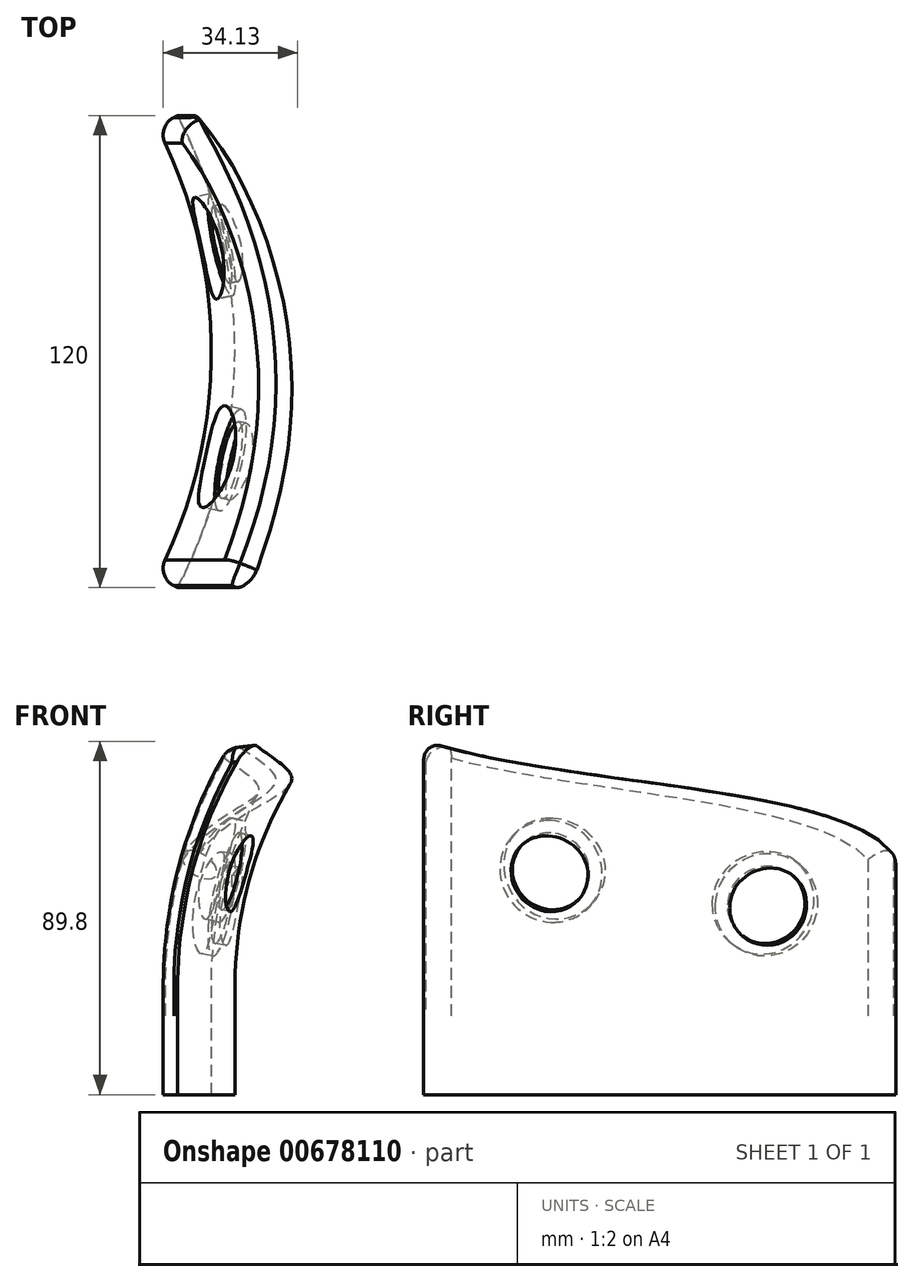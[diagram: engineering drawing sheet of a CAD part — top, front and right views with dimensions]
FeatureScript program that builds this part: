
annotation { "Feature Type Name" : "Feature", "Feature Type Description" : "" }
export const myFeature = defineFeature(function(context is Context, id is Id, definition is map)
    precondition{}
    {
        {
            var Q0;
            Q0=qCreatedBy(makeId("Top.planeOp"),FACE);
            var sketch = newSketch(context, id + "F0", { "sketchPlane" : qUnion([Q0])});
            skCircle(sketch, "E0", {"center": v(0, 0) * mm, "radius": 125 * mm});
            skCircle(sketch, "E1", {"center": v(0, 0) * mm, "radius": 131 * mm});
            skLineSegment(sketch, "E2", {"start": v(0, 0) * mm, "end": v(116.45, 60) * mm});
            skLineSegment(sketch, "E3", {"start": v(0, 0) * mm, "end": v(116.45, -60) * mm});
            skLineSegment(sketch, "E4", {"start": v(116.45, -60) * mm, "end": v(116.45, 60) * mm, "construction": true});
            skPoint(sketch, "E5", {"position": v(125, 0) * mm});
            skLineSegment(sketch, "E6", {"start": v(0, 0) * mm, "end": v(167.42, 0) * mm, "construction": true});
            skPoint(sketch, "E6.endSnap0", {"position": v(116.45, 0) * mm});
            skLineSegment(sketch, "E7", {"start": v(0, 0) * mm, "end": v(290.04, 61.65) * mm, "construction": true});
            skLineSegment(sketch, "E8", {"start": v(0, 0) * mm, "end": v(279.85, -59.48) * mm, "construction": true});
            skLineSegment(sketch, "E9", {"start": v(0, 0) * mm, "end": v(22.15, 104.2) * mm, "construction": true});
            skLineSegment(sketch, "E10", {"start": v(0, 0) * mm, "end": v(-22.73, 106.95) * mm, "construction": true});
            skSolve(sketch);
        }
        {
            var Q0;
            Q0=qCreatedBy(makeId("Front.planeOp"),FACE);
            var sketch = newSketch(context, id + "F1", { "sketchPlane" : qUnion([Q0])});
            skLineSegment(sketch, "E11.0", {"start": v(-125, 0) * mm, "end": v(125, 0) * mm, "construction": true});
            skLineSegment(sketch, "E12.0", {"start": v(-131, 0) * mm, "end": v(131, 0) * mm, "construction": true});
            skPoint(sketch, "E13.0", {"position": v(116.45, 0) * mm});
            skLineSegment(sketch, "E14", {"start": v(125, 0) * mm, "end": v(131, 0) * mm, "construction": true});
            skPoint(sketch, "E15", {"position": v(128, 0) * mm});
            skFitSpline(sketch, "E16", {"points": [v(128, 0) * mm, v(128, 5.95) * mm, v(153, 75) * mm], "startDerivative": vector(0, 39.53) * mm, "endDerivative": vector(96.35, 111.36) * mm});
            skLineSegment(sketch, "E17", {"start": v(128, 0) * mm, "end": v(128, 92.21) * mm, "construction": true});
            skLineSegment(sketch, "E18", {"start": v(128, 0) * mm, "end": v(128, -20) * mm, "construction": true});
            skLineSegment(sketch, "E19", {"start": v(149.6, 60.4) * mm, "end": v(80.14, 60.4) * mm, "construction": true});
            skLineSegment(sketch, "E20", {"start": v(128, 0) * mm, "end": v(153, 75) * mm, "construction": true});
            skLineSegment(sketch, "E21", {"start": v(135.36, 46.04) * mm, "end": v(0, 99.87) * mm, "construction": true});
            skLineSegment(sketch, "E22", {"start": v(0, 0) * mm, "end": v(0, 121.22) * mm, "construction": true});
            skLineSegment(sketch, "E23", {"start": v(0, 0) * mm, "end": v(20.37, 115.5) * mm, "construction": true});
            skPoint(sketch, "E24", {"position": v(135.36, 46.04) * mm});
            skLineSegment(sketch, "E25", {"start": v(135.36, 46.04) * mm, "end": v(125, 20) * mm, "construction": true});
            skPoint(sketch, "E26", {"position": v(128.4, 16.37) * mm});
            skLineSegment(sketch, "E27", {"start": v(128.4, 16.37) * mm, "end": v(127.55, 6.42) * mm, "construction": true});
            skLineSegment(sketch, "E28", {"start": v(128.4, 16.37) * mm, "end": v(0, 27.32) * mm, "construction": true});
            skLineSegment(sketch, "E29", {"start": v(0, 0) * mm, "end": v(28.87, 125.04) * mm, "construction": true});
            skSolve(sketch);
        }
        {
            var Q0;
            {var subQ0=sQuery(id+"F0.wireOp",EDGE,"E2");var subQ1=sQuery(id+"F0.wireOp",EDGE,"E0");var subQ2=makeQuery(id+"F0.imprint","INTERSECT",VERTEX,{"derivedFrom":[subQ1,subQ0]});Q0=makeQuery(id+"F0.imprint","IMPRINT",FACE,{"disambiguationData":[TD([[makeQuery(id+"F0.imprint","IMPRINT",EDGE,{"disambiguationData":[TD([[subQ2,1.0]])],"derivedFrom":subQ1}),-1.0]])]});}
            var Q1;
            Q1=sQuery(id+"F1.wireOp",EDGE,"E16");
            sweep(context, id + "F2", {"profiles" : qUnion([Q0]), "path" : qUnion([Q1])});
        }
        {
            var Q0;
            Q0=makeQuery(id+"F2.opSweep","SWEPT_EDGE",EDGE,{"disambiguationData":[OSD([sQuery(id+"F0.wireOp",EDGE,"E1"),sQuery(id+"F0.wireOp",EDGE,"E3"),sQuery(id+"F1.wireOp",EDGE,"E16")])]});
            cPoint(context, id + "F3", {"entities" : qUnion([Q0]), "parameter" : 0.5});
        }
        {
            var Q0;
            Q0=qCreatedBy(makeId("Front.planeOp"),FACE);
            var Q1;
            Q1=qCreatedBy(id+"F3",VERTEX);
            cPlane(context, id + "F4", {"entities" : qUnion([Q0, Q1]), "cplaneType" : CPlaneType.PLANE_POINT, "offset" : 25 * mm, "width" : 150 * mm, "height" : 150 * mm});
        }
        {
            var Q0;
            Q0=qCreatedBy(id+"F4.planeOp",FACE);
            var sketch = newSketch(context, id + "F5", { "sketchPlane" : qUnion([Q0])});
            skLineSegment(sketch, "E30", {"start": v(16.14, 70) * mm, "end": v(342.74, 70) * mm});
            skLineSegment(sketch, "E31.top", {"start": v(16.14, 220) * mm, "end": v(342.74, 220) * mm});
            skLineSegment(sketch, "E31.left", {"start": v(16.14, 70) * mm, "end": v(16.14, 220) * mm});
            skLineSegment(sketch, "E31.right", {"start": v(342.74, 70) * mm, "end": v(342.74, 220) * mm});
            skSolve(sketch);
        }
        {
            var Q0;
            Q0=qCreatedBy(makeId("Right.planeOp"),FACE);
            var sketch = newSketch(context, id + "F6", { "sketchPlane" : qUnion([Q0])});
            skPoint(sketch, "E32.0", {"position": v(-60, 70) * mm});
            skLineSegment(sketch, "E33", {"start": v(-74, 70) * mm, "end": v(-141.5, 70) * mm, "construction": true});
            skFitSpline(sketch, "E34.0", {"points": [v(50, 0) * mm, v(1000, 50) * mm, v(2.92, 1000) * mm, v(50, 3.5) * mm, v(1000, 50) * mm, v(7.03, 1000) * mm, v(50, 8.56) * mm, v(1000, 50) * mm, v(12.28, 1000) * mm, v(50, 14.48) * mm, v(1000, 50) * mm, v(21.9, 1000) * mm], "construction": true});
            skFitSpline(sketch, "E35.0", {"points": [v(-50, 0) * mm, v(1000, -50) * mm, v(2.92, 1000) * mm, v(-50, 3.5) * mm, v(1000, -50) * mm, v(7.03, 1000) * mm, v(-50, 8.56) * mm, v(1000, -50) * mm, v(12.28, 1000) * mm, v(-50, 14.48) * mm, v(1000, -50) * mm, v(21.9, 1000) * mm], "construction": true});
            skLineSegment(sketch, "E36", {"start": v(68.45, 40) * mm, "end": v(-5.43, 40) * mm, "construction": true});
            skLineSegment(sketch, "E37", {"start": v(-55, 57) * mm, "end": v(-106.26, 57) * mm, "construction": true});
            skFitSpline(sketch, "E38", {"points": [v(60, 40) * mm, v(-60, 70) * mm], "startDerivative": vector(-33.37, 57.1) * mm, "endDerivative": vector(-107.54, 36.27) * mm});
            skPoint(sketch, "E39", {"position": v(-80.63, 57) * mm});
            skSolve(sketch);
        }
        {
            var Q0;
            Q0=makeQuery(id+"F5.imprint","IMPRINT",FACE,{"disambiguationData":[TD([[makeQuery(id+"F5.imprint","IMPRINT",EDGE,{"derivedFrom":sQuery(id+"F5.wireOp",EDGE,"E30")}),1.0]])]});
            var Q1;
            Q1=sQuery(id+"F6.wireOp",EDGE,"E38");
            sweep(context, id + "F7", {"operationType" : NewBodyOperationType.REMOVE, "profiles" : qUnion([Q0]), "path" : qUnion([Q1]), "keepProfileOrientation" : true});
        }
        {
            var Q0;
            Q0=makeQuery(id+"F7.boolean.opBoolean","INTERSECT",EDGE,{"derivedFrom":[makeQuery(id+"F2.opSweep","SWEPT_FACE",FACE,{"disambiguationData":[OSD([sQuery(id+"F0.wireOp",EDGE,"E0"),sQuery(id+"F1.wireOp",EDGE,"E16")])]}),makeQuery(id+"F7.opSweep","SWEPT_FACE",FACE,{"disambiguationData":[OSD([sQuery(id+"F5.wireOp",EDGE,"E30"),sQuery(id+"F6.wireOp",EDGE,"E38")])]})]});
            fillet(context, id + "F8", {"entities" : qUnion([Q0]), "radius" : 5 * mm, "tangentPropagation" : true, "allowEdgeOverflow" : false});
        }
        {
            var Q0;
            Q0=makeQuery(id+"F2.opSweep","SWEPT_EDGE",EDGE,{"disambiguationData":[OSD([sQuery(id+"F0.wireOp",EDGE,"E0"),sQuery(id+"F0.wireOp",EDGE,"E2"),sQuery(id+"F1.wireOp",EDGE,"E16")])]});
            var Q1;
            Q1=makeQuery(id+"F2.opSweep","SWEPT_EDGE",EDGE,{"disambiguationData":[OSD([sQuery(id+"F0.wireOp",EDGE,"E0"),sQuery(id+"F0.wireOp",EDGE,"E3"),sQuery(id+"F1.wireOp",EDGE,"E16")])]});
            fillet(context, id + "F9", {"entities" : qUnion([Q0, Q1]), "radius" : 5 * mm, "tangentPropagation" : true, "allowEdgeOverflow" : false});
        }
        {
            var Q0;
            Q0=qCreatedBy(makeId("Front.planeOp"),FACE);
            var sketch = newSketch(context, id + "F10", { "sketchPlane" : qUnion([Q0])});
            skLineSegment(sketch, "E40", {"start": v(0, 0) * mm, "end": v(178.06, -4.84) * mm, "construction": true});
            skSolve(sketch);
        }
        {
            var Q0;
            Q0=sQuery(id+"F0.wireOp",VERTEX,"E2.start");
            var Q1;
            Q1=sQuery(id+"F10.wireOp",EDGE,"E40");
            cPlane(context, id + "F11", {"entities" : qUnion([Q0, Q1]), "cplaneType" : CPlaneType.LINE_POINT, "offset" : 0 * mm, "width" : 150 * mm, "height" : 150 * mm});
        }
        {
            var Q0;
            Q0=sQuery(id+"F0.wireOp",EDGE,"E7");
            var Q1;
            Q1=sQuery(id+"F0.wireOp",VERTEX,"E2.start");
            cPlane(context, id + "F12", {"entities" : qUnion([Q0, Q1]), "cplaneType" : CPlaneType.LINE_POINT, "offset" : 25 * mm, "width" : 150 * mm, "height" : 150 * mm});
        }
        {
            var Q0;
            Q0=sQuery(id+"F0.wireOp",VERTEX,"E2.start");
            var Q1;
            Q1=sQuery(id+"F0.wireOp",EDGE,"E8");
            cPlane(context, id + "F13", {"entities" : qUnion([Q0, Q1]), "cplaneType" : CPlaneType.LINE_POINT, "offset" : 25 * mm, "width" : 150 * mm, "height" : 150 * mm});
        }
        {
            var Q0;
            Q0=makeQuery(id+"F2.opSweep","CAP_FACE",FACE,{"disambiguationData":[OSD([sQuery(id+"F0.wireOp",EDGE,"E0"),sQuery(id+"F0.wireOp",EDGE,"E1"),sQuery(id+"F0.wireOp",EDGE,"E2"),sQuery(id+"F0.wireOp",EDGE,"E3"),sQuery(id+"F1.wireOp",VERTEX,"E16.start")])],"isStart":true});
            var sketch = newSketch(context, id + "F14", { "sketchPlane" : qUnion([Q0])});
            skLineSegment(sketch, "E41.0.0", {"start": v(116.45, 60) * mm, "end": v(115.48, 59.5) * mm});
            skArc(sketch, "E41.0.1", {"start": v(115.48, 59.5) * mm, "mid": v(113.04, 56.67) * mm, "end": v(113.24, 52.94) * mm});
            skArc(sketch, "E41.0.2", {"start": v(113.24, -52.94) * mm, "mid": v(125, 0) * mm, "end": v(113.24, 52.94) * mm});
            skArc(sketch, "E41.0.3", {"start": v(113.24, -52.94) * mm, "mid": v(113.04, -56.67) * mm, "end": v(115.48, -59.5) * mm});
            skLineSegment(sketch, "E41.0.4", {"start": v(116.45, -60) * mm, "end": v(115.48, -59.5) * mm});
            skArc(sketch, "E41.0.5", {"start": v(116.45, -60) * mm, "mid": v(131, 0) * mm, "end": v(116.45, 60) * mm});
            skSolve(sketch);
        }
        {
            var Q0;
            Q0=makeQuery(id+"F14.imprint","IMPRINT",FACE,{"disambiguationData":[TD([[makeQuery(id+"F14.imprint","IMPRINT",EDGE,{"derivedFrom":sQuery(id+"F14.wireOp",EDGE,"E41.0.0")}),-1.0]])]});
            extrude(context, id + "F15", {"entities" : qUnion([Q0]), "operationType" : NewBodyOperationType.ADD, "depth" : 20 * mm, "offsetDistance" : 25 * mm});
        }
        {
            var Q0;
            Q0=sQuery(id+"F0.wireOp",VERTEX,"E10.end");
            var Q1;
            Q1=sQuery(id+"F1.wireOp",VERTEX,"E23.end");
            var Q2;
            Q2=sQuery(id+"F0.wireOp",VERTEX,"E2.start");
            cPlane(context, id + "F16", {"entities" : qUnion([Q0, Q1, Q2]), "cplaneType" : CPlaneType.THREE_POINT, "offset" : 25 * mm, "width" : 150 * mm, "height" : 150 * mm});
        }
        {
            var Q0;
            Q0=sQuery(id+"F0.wireOp",VERTEX,"E9.end");
            var Q1;
            Q1=sQuery(id+"F0.wireOp",VERTEX,"E2.start");
            var Q2;
            Q2=sQuery(id+"F1.wireOp",VERTEX,"E29.end");
            cPlane(context, id + "F17", {"entities" : qUnion([Q0, Q1, Q2]), "cplaneType" : CPlaneType.THREE_POINT, "offset" : 25 * mm, "width" : 150 * mm, "height" : 150 * mm});
        }
        {
            var Q0;
            Q0=qCreatedBy(id+"F16.planeOp",FACE);
            var sketch = newSketch(context, id + "F18", { "sketchPlane" : qUnion([Q0])});
            skCircle(sketch, "E42", {"center": v(-1.8, 50) * mm, "radius": 10 * mm});
            skCircle(sketch, "E43", {"center": v(-1.8, 50) * mm, "radius": 13.25 * mm});
            skLineSegment(sketch, "E44.0", {"start": v(0, 0) * mm, "end": v(-1.82, 50.36) * mm, "construction": true});
            skSolve(sketch);
        }
        {
            var Q0;
            Q0=qCreatedBy(id+"F17.planeOp",FACE);
            var sketch = newSketch(context, id + "F19", { "sketchPlane" : qUnion([Q0])});
            skLineSegment(sketch, "E45.0", {"start": v(0, 0) * mm, "end": v(-2.95, 62.95) * mm, "construction": true});
            skCircle(sketch, "E46", {"center": v(-3.04, 65) * mm, "radius": 10 * mm});
            skCircle(sketch, "E47", {"center": v(-3.04, 65) * mm, "radius": 13.25 * mm});
            skSolve(sketch);
        }
        {
            var Q0;
            Q0=makeQuery(id+"F19.imprint","IMPRINT",FACE,{"disambiguationData":[TD([[makeQuery(id+"F19.imprint","IMPRINT",EDGE,{"derivedFrom":sQuery(id+"F19.wireOp",EDGE,"E46")}),1.0]])]});
            var Q1;
            Q1=makeQuery(id+"F2.opSweep","SWEPT_BODY",BODY,{"disambiguationData":[OSD([sQuery(id+"F0.wireOp",EDGE,"E0"),sQuery(id+"F0.wireOp",EDGE,"E1"),sQuery(id+"F0.wireOp",EDGE,"E2"),sQuery(id+"F0.wireOp",EDGE,"E3"),sQuery(id+"F1.wireOp",EDGE,"E16")])]});
            extrude(context, id + "F20", {"entities" : qUnion([Q0]), "operationType" : NewBodyOperationType.REMOVE, "endBound" : BoundingType.UP_TO_BODY, "depth" : 25 * mm, "endBoundEntityBody" : qUnion([Q1]), "hasOffset" : true, "offsetDistance" : 10 * mm, "offsetOppositeDirection" : true});
        }
        {
            var Q0;
            Q0=makeQuery(id+"F18.imprint","IMPRINT",FACE,{"disambiguationData":[TD([[makeQuery(id+"F18.imprint","IMPRINT",EDGE,{"derivedFrom":sQuery(id+"F18.wireOp",EDGE,"E42")}),1.0]])]});
            var Q1;
            Q1=makeQuery(id+"F2.opSweep","SWEPT_BODY",BODY,{"disambiguationData":[OSD([sQuery(id+"F0.wireOp",EDGE,"E0"),sQuery(id+"F0.wireOp",EDGE,"E1"),sQuery(id+"F0.wireOp",EDGE,"E2"),sQuery(id+"F0.wireOp",EDGE,"E3"),sQuery(id+"F1.wireOp",EDGE,"E16")])]});
            extrude(context, id + "F21", {"entities" : qUnion([Q0]), "operationType" : NewBodyOperationType.REMOVE, "endBound" : BoundingType.UP_TO_BODY, "oppositeDirection" : true, "depth" : 25 * mm, "endBoundEntityBody" : qUnion([Q1]), "hasOffset" : true, "offsetDistance" : 10 * mm, "offsetOppositeDirection" : true});
        }
        {
            var Q0;
            Q0=makeQuery(id+"F18.imprint","IMPRINT",FACE,{"disambiguationData":[TD([[makeQuery(id+"F18.imprint","IMPRINT",EDGE,{"derivedFrom":sQuery(id+"F18.wireOp",EDGE,"E42")}),-1.0]])]});
            var Q1;
            Q1=makeQuery(id+"F2.opSweep","SWEPT_BODY",BODY,{"disambiguationData":[OSD([sQuery(id+"F0.wireOp",EDGE,"E0"),sQuery(id+"F0.wireOp",EDGE,"E1"),sQuery(id+"F0.wireOp",EDGE,"E2"),sQuery(id+"F0.wireOp",EDGE,"E3"),sQuery(id+"F1.wireOp",EDGE,"E16")])]});
            extrude(context, id + "F22", {"entities" : qUnion([Q0]), "operationType" : NewBodyOperationType.REMOVE, "oppositeDirection" : true, "depth" : (119.8 + 4) * mm, "endBoundEntityBody" : qUnion([Q1]), "hasOffset" : true, "offsetDistance" : 3 * mm, "offsetOppositeDirection" : true});
        }
        {
            var Q0;
            Q0=makeQuery(id+"F19.imprint","IMPRINT",FACE,{"disambiguationData":[TD([[makeQuery(id+"F19.imprint","IMPRINT",EDGE,{"derivedFrom":sQuery(id+"F19.wireOp",EDGE,"E46")}),-1.0]])]});
            var Q1;
            Q1=makeQuery(id+"F2.opSweep","SWEPT_BODY",BODY,{"disambiguationData":[OSD([sQuery(id+"F0.wireOp",EDGE,"E0"),sQuery(id+"F0.wireOp",EDGE,"E1"),sQuery(id+"F0.wireOp",EDGE,"E2"),sQuery(id+"F0.wireOp",EDGE,"E3"),sQuery(id+"F1.wireOp",EDGE,"E16")])]});
            extrude(context, id + "F23", {"entities" : qUnion([Q0]), "operationType" : NewBodyOperationType.REMOVE, "depth" : (117.2 + 4.2) * mm, "endBoundEntityBody" : qUnion([Q1]), "hasOffset" : true, "offsetDistance" : 3 * mm, "offsetOppositeDirection" : true});
        }
    });
